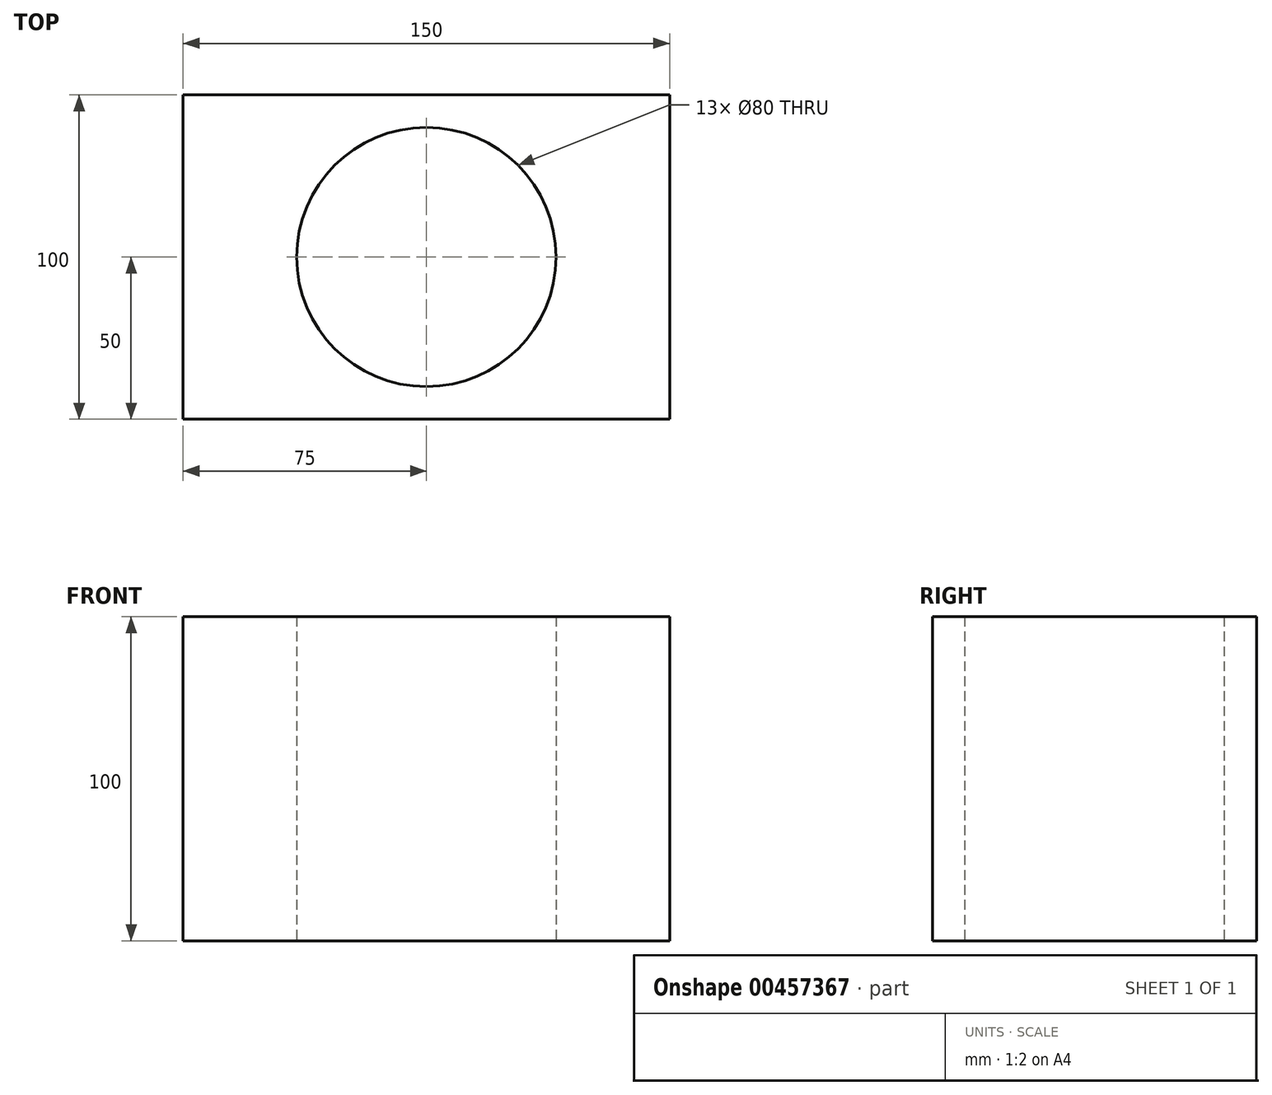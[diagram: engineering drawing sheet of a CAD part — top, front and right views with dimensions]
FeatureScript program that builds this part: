
annotation { "Feature Type Name" : "Feature", "Feature Type Description" : "" }
export const myFeature = defineFeature(function(context is Context, id is Id, definition is map)
    precondition{}
    {
        {
            var Q0;
            Q0=qCreatedBy(makeId("Top.planeOp"),FACE);
            var sketch = newSketch(context, id + "F0", { "sketchPlane" : qUnion([Q0])});
            skLineSegment(sketch, "E0.bottom", {"start": v(75, -50) * mm, "end": v(-75, -50) * mm});
            skLineSegment(sketch, "E0.top", {"start": v(75, 50) * mm, "end": v(-75, 50) * mm});
            skLineSegment(sketch, "E0.left", {"start": v(75, -50) * mm, "end": v(75, 50) * mm});
            skLineSegment(sketch, "E0.right", {"start": v(-75, -50) * mm, "end": v(-75, 50) * mm});
            skPoint(sketch, "E0.middle", {"position": v(0, 0) * mm});
            skCircle(sketch, "E1", {"center": v(0, 0) * mm, "radius": 40 * mm});
            skLineSegment(sketch, "E2", {"start": v(0, 40) * mm, "end": v(0, -40) * mm, "construction": true});
            skSolve(sketch);
        }
        {
            var Q0;
            Q0 = qSketchRegion(id + "F0", true);
            extrude(context, id + "F1", {"entities" : qUnion([Q0]), "depth" : 100 * mm});
        }
    });
